# Revit family: Faucet-Bath_Filler-KOHLER-OCCASION-K-27016_1
name_source: partatom
category: Plumbing Fixtures
revit_build: Autodesk Revit 2017 (Build: 20160225_1515(x64)
units: mm (PartAtom-declared; Revit-internal decimal feet)

## family parameters
Cut with Voids When Loaded = No
Host = Face
OmniClass Number = 23.31.11.00
OmniClass Title = Faucets
Part Type = Normal
Room Calculation Point = No
Round Connector Dimension = Use Diameter
Shared = No

## types (5) — shared parameters
ADA Compliant = No
Assembly Code = D2010
CW Connection = No
Cold Water Inlet = Cold Water Inlet
Date Modified = 02/15/2021
Default Elevation = 36"
Description = CLASSICAL DECK MOUNT BATH FILLER C- SHAPE SPOUT
Drain Included = No
Faucet Hole Spacing = 0"
Flow Rate = 0 GPM
HW Connection = No
Handle Clearance = 0"
Height = 12 7/16"
Hot Water Inlet = Hot Water Inlet
Length = 7 13/16"
Manufacturer = KOHLER Co.
Master Format 2014 = 22 41 39
Master Format 2014 Name = Residential Faucets, Supplies, and Trim
Material = Brass Construction
Pressure = 0.00 psi
Product Documentation Link = https://www.us.kohler.com
Product Name = OCCASION
Product Page URL = http://www.us.kohler.com
Spout Reach = 7 13/16"
URL = https://www.us.kohler.com
Vent Connection = No
Waste Connection = No
Waste Water Outlet = Waste Water Outlet
WaterSense Certified = No
Width = 2 3/4"

## per-type parameters (varying)
| type | Finish | Model | Type |
| CP- Polished Chrome | Kohler-Metal-CP-Polished_Chrome | K-27016-CP | 1 |
| BN- Vibrant Brushed Nickel | Kohler-Metal-BN-Vibrant_Brushed_Nickel | K-27016-BN | 2 |
| BL- Matte Black | Kohler-Metal-BL-Matte_Black | K-27016-BL | 3 |
| 2MB- Vibrant Brushed Moderne Brass | Kohler-Metal-2MB-Vibrant_Brushed_Moderne_Brass | K-27016-2MB | 4 |
| SN- Vibrant Polished Nickel | Kohler-Metal-SN-Vibrant_Polished_Nickel | K-27016-SN | 5 |

## geometry (parser evidence)
native form markers: Sweep x5
no freeform markers — native parametric forms only
